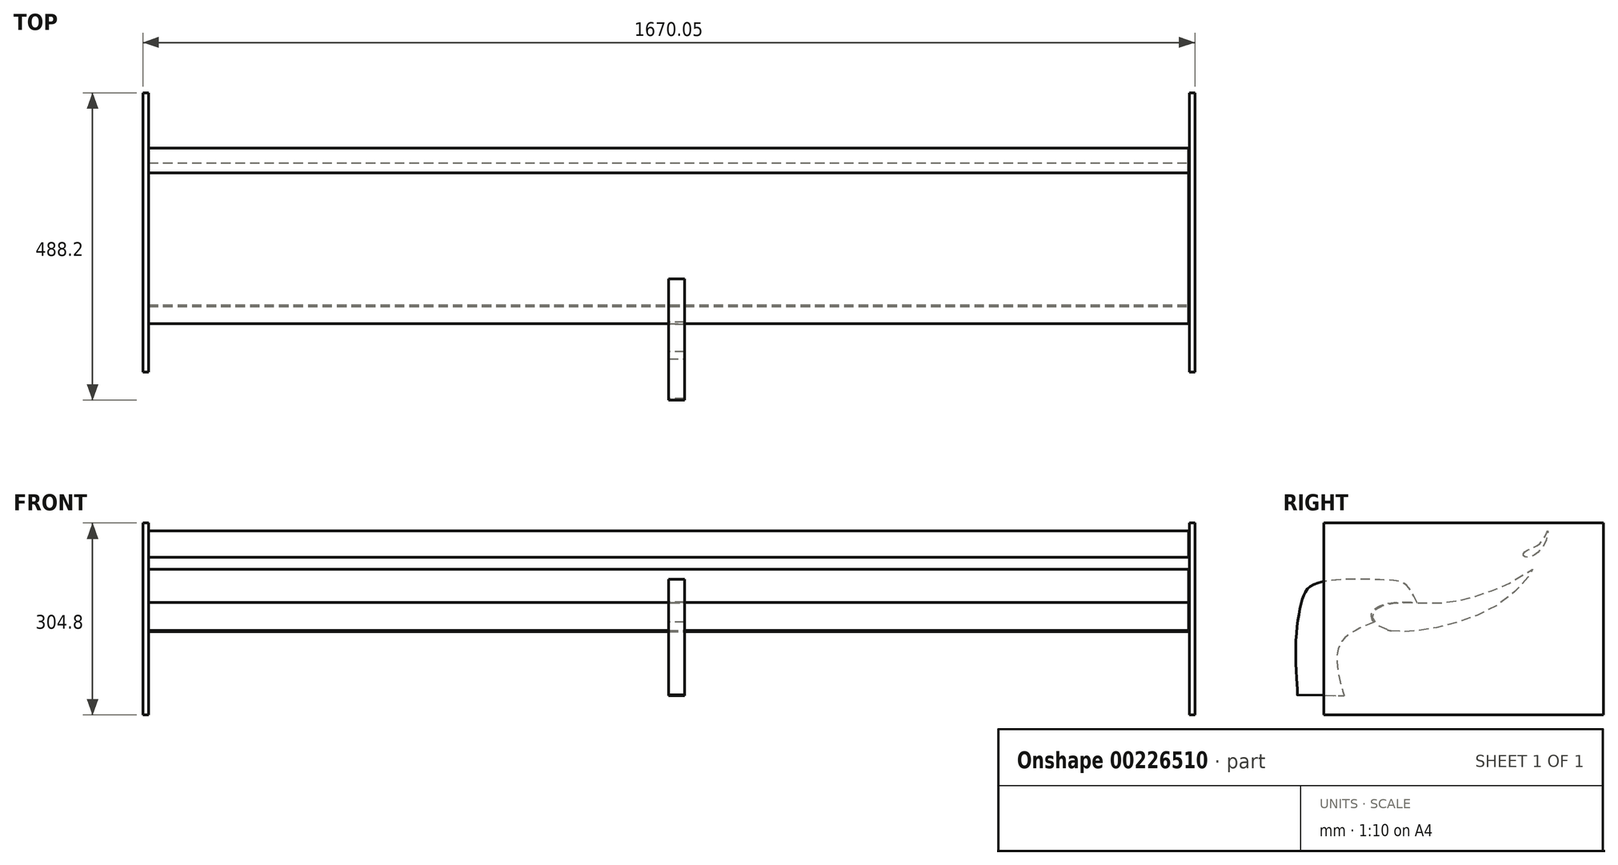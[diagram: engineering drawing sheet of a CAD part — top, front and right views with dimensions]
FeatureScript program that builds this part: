
annotation { "Feature Type Name" : "Feature", "Feature Type Description" : "" }
export const myFeature = defineFeature(function(context is Context, id is Id, definition is map)
    precondition{}
    {
        {
            var Q0;
            Q0=qCreatedBy(makeId("Right.planeOp"),FACE);
            var sketch = newSketch(context, id + "F0", { "sketchPlane" : qUnion([Q0])});
            skFitSpline(sketch, "E0", {"points": [v(-141.73, 9.76) * mm, v(-127.34, 20.87) * mm, v(-94.7, 26.1) * mm, v(-34.32, 25.76) * mm, v(14.93, 34.25) * mm, v(88.44, 64.17) * mm, v(112.46, 78.97) * mm, v(79.53, 39.46) * mm, v(-12.9, -6.97) * mm, v(-88.3, -19.83) * mm, v(-118.45, -17.15) * mm, v(-138.56, -5.56) * mm, v(-141.73, 9.76) * mm]});
            skFitSpline(sketch, "E1", {"points": [v(-118.45, -17.15) * mm, v(-112.85, -18.51) * mm], "startDerivative": vector(10.2, -1.83) * mm, "endDerivative": vector(10.2, -1.83) * mm});
            skFitSpline(sketch, "E2", {"points": [v(97.32, 100.73) * mm, v(99.67, 106.74) * mm, v(113.01, 113.54) * mm, v(128.19, 125.05) * mm, v(136.3, 139.96) * mm, v(133.42, 125.31) * mm, v(122.95, 108.57) * mm, v(106.74, 98.37) * mm, v(97.32, 100.73) * mm]});
            skSolve(sketch);
        }
        {
            var Q0;
            Q0 = qSketchRegion(id + "F0", true);
            extrude(context, id + "F1", {"entities" : qUnion([Q0]), "endBound" : BoundingType.SYMMETRIC, "depth" : 1651 * mm});
        }
        {
            var Q0;
            Q0=qCreatedBy(makeId("Top.planeOp"),FACE);
            var sketch = newSketch(context, id + "F2", { "sketchPlane" : qUnion([Q0])});
            skLineSegment(sketch, "E3.bottom", {"start": v(-834.52, 224.24) * mm, "end": v(-825.45, 224.24) * mm});
            skLineSegment(sketch, "E3.top", {"start": v(-834.52, -219.22) * mm, "end": v(-825.45, -219.22) * mm});
            skLineSegment(sketch, "E3.left", {"start": v(-834.52, 224.24) * mm, "end": v(-834.52, -219.22) * mm});
            skLineSegment(sketch, "E3.right", {"start": v(-825.45, 224.24) * mm, "end": v(-825.45, -219.22) * mm});
            skLineSegment(sketch, "E4.bottom", {"start": v(826.46, -219.22) * mm, "end": v(835.53, -219.22) * mm});
            skLineSegment(sketch, "E4.top", {"start": v(826.46, 224.24) * mm, "end": v(835.53, 224.24) * mm});
            skLineSegment(sketch, "E4.left", {"start": v(826.46, -219.22) * mm, "end": v(826.46, 224.24) * mm});
            skLineSegment(sketch, "E4.right", {"start": v(835.53, -219.22) * mm, "end": v(835.53, 224.24) * mm});
            skSolve(sketch);
        }
        {
            var Q0;
            Q0 = qSketchRegion(id + "F2", true);
            extrude(context, id + "F3", {"entities" : qUnion([Q0]), "endBound" : BoundingType.SYMMETRIC, "depth" : 304.8 * mm});
        }
        {
            var Q0;
            Q0=qCreatedBy(makeId("Right.planeOp"),FACE);
            var sketch = newSketch(context, id + "F4", { "sketchPlane" : qUnion([Q0])});
            skFitSpline(sketch, "E5", {"points": [v(-71.22, 26.45) * mm, v(-89.65, 54.88) * mm, v(-121.82, 62.07) * mm, v(-231.47, 56.76) * mm, v(-253.03, 32.7) * mm, v(-263.96, -51.96) * mm, v(-261.46, -120.68) * mm, v(-261.78, -120.37) * mm], "startDerivative": vector(-132.58, 266.54) * mm, "endDerivative": vector(-23.65, 37.4) * mm});
            skFitSpline(sketch, "E6", {"points": [v(-139.63, -4.47) * mm, v(-193.99, -41.02) * mm, v(-194.3, -95.7) * mm, v(-187.11, -121.62) * mm], "startDerivative": vector(-175.19, -72.56) * mm, "endDerivative": vector(27.88, -89.22) * mm});
            skFitSpline(sketch, "E7", {"points": [v(-139.63, -4.47) * mm, v(-142.75, 0) * mm, v(-143.07, 10.21) * mm, v(-132.76, 19.9) * mm, v(-113.39, 25.52) * mm, v(-94.65, 26.77) * mm, v(-71.22, 26.45) * mm], "startDerivative": vector(-34.04, 36.83) * mm, "endDerivative": vector(114.86, -2.63) * mm});
            skFitSpline(sketch, "E8", {"points": [v(-261.78, -120.37) * mm, v(-187.11, -121.62) * mm], "startDerivative": vector(74.66, -1.25) * mm, "endDerivative": vector(74.66, -1.25) * mm});
            skSolve(sketch);
        }
        {
            var Q0;
            Q0 = qSketchRegion(id + "F4", true);
            extrude(context, id + "F5", {"entities" : qUnion([Q0]), "depth" : 25.4 * mm});
        }
    });
